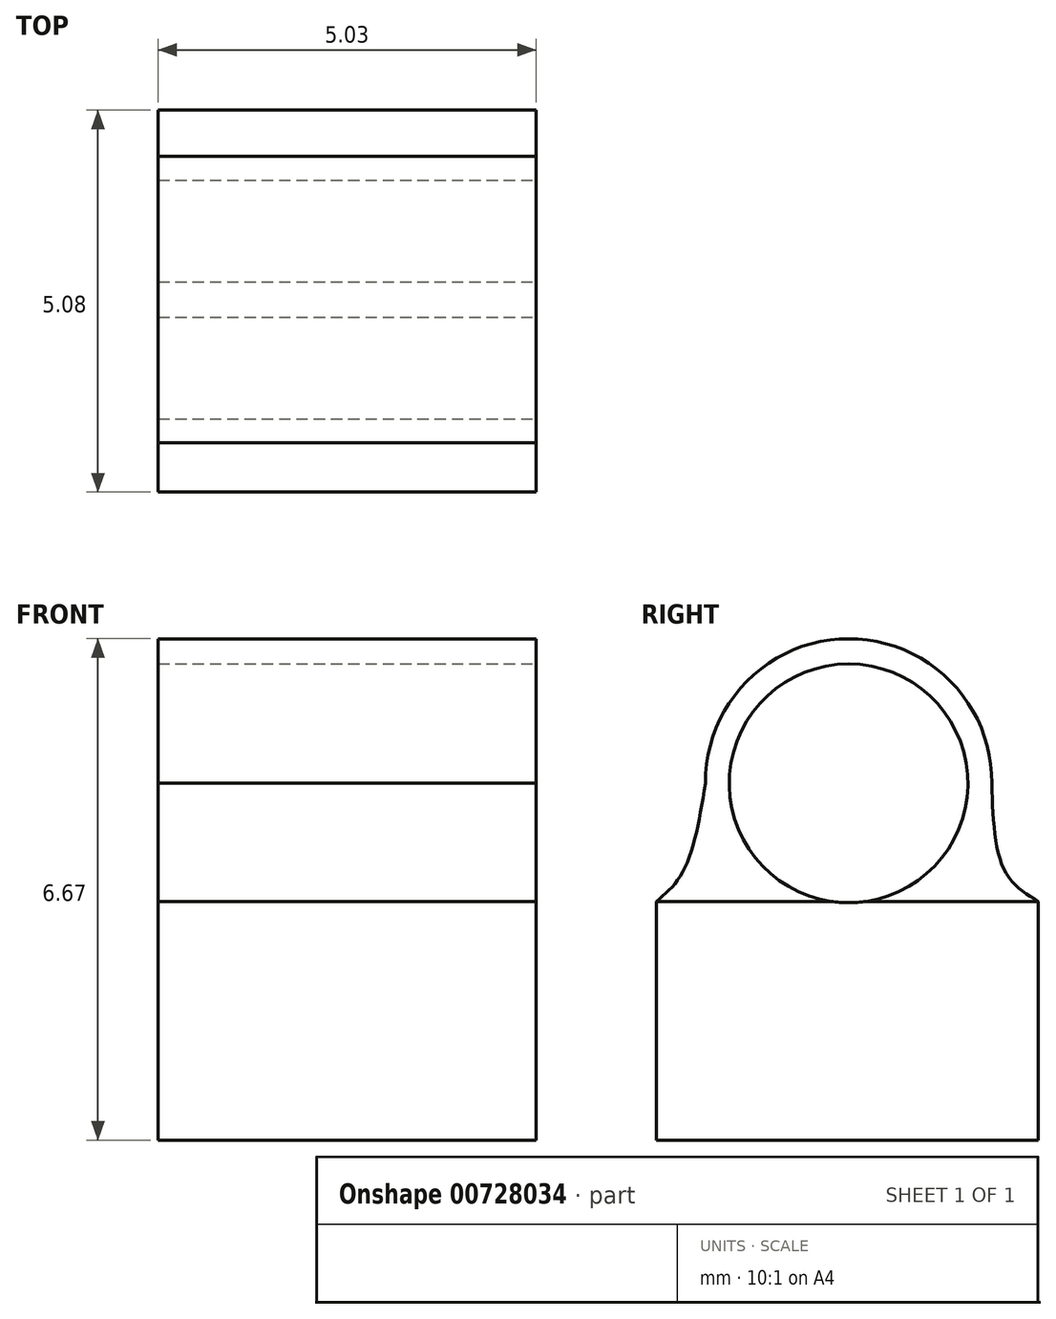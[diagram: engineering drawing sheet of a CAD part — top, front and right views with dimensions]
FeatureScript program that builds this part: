
annotation { "Feature Type Name" : "Feature", "Feature Type Description" : "" }
export const myFeature = defineFeature(function(context is Context, id is Id, definition is map)
    precondition{}
    {
        {
            var Q0;
            Q0=qCreatedBy(makeId("Top.planeOp"),FACE);
            var sketch = newSketch(context, id + "F0", { "sketchPlane" : qUnion([Q0])});
            skLineSegment(sketch, "E0.bottom", {"start": v(0, 0) * mm, "end": v(5.03, 0) * mm});
            skLineSegment(sketch, "E0.top", {"start": v(0, 5.08) * mm, "end": v(5.03, 5.08) * mm});
            skLineSegment(sketch, "E0.left", {"start": v(0, 0) * mm, "end": v(0, 5.08) * mm});
            skLineSegment(sketch, "E0.right", {"start": v(5.03, 0) * mm, "end": v(5.03, 5.08) * mm});
            skSolve(sketch);
        }
        {
            var Q0;
            Q0 = qSketchRegion(id + "F0", true);
            extrude(context, id + "F1", {"entities" : qUnion([Q0]), "depth" : 3.17 * mm, "offsetDistance" : 25.4 * mm});
        }
        {
            var Q0;
            Q0=makeQuery(id+"F1.opExtrude","SWEPT_FACE",FACE,{"disambiguationData":[OSD([sQuery(id+"F0.wireOp",EDGE,"E0.right")])]});
            var sketch = newSketch(context, id + "F2", { "sketchPlane" : qUnion([Q0])});
            skPoint(sketch, "E1.first.point", {"position": v(2.54, 3.18) * mm});
            skPoint(sketch, "E1.second.point", {"position": v(2.54, 6.35) * mm});
            skPoint(sketch, "E1.second.point.positionSnap0", {"position": v(2.54, 3.18) * mm});
            skPoint(sketch, "E1.third.point", {"position": v(0.97, 4.75) * mm});
            skArc(sketch, "E2", {"start": v(4.46, 4.75) * mm, "mid": v(2.56, 6.67) * mm, "end": v(0.65, 4.75) * mm});
            skFitSpline(sketch, "E3", {"points": [v(0, 3.18) * mm, v(0.36, 3.58) * mm, v(0.65, 4.75) * mm], "startDerivative": vector(0.97, 0.82) * mm, "endDerivative": vector(0.37, 2.22) * mm});
            skFitSpline(sketch, "E4", {"points": [v(5.08, 3.18) * mm, v(4.63, 3.58) * mm, v(4.46, 4.75) * mm], "startDerivative": vector(-1.23, 0.76) * mm, "endDerivative": vector(-0.07, 2.3) * mm});
            skSolve(sketch);
        }
        {
            var Q0;
            Q0 = qSketchRegion(id + "F2", true);
            var Q1;
            Q1=makeQuery(id+"F2.imprint","IMPRINT",FACE,{"disambiguationData":[TD([[makeQuery(id+"F2.imprint","IMPRINT",EDGE,{"derivedFrom":sQuery(id+"F2.wireOp",EDGE,"E2")}),1.0]])]});
            extrude(context, id + "F3", {"entities" : qUnion([Q0, Q1]), "oppositeDirection" : true, "depth" : 5.03 * mm, "offsetDistance" : 25.4 * mm});
        }
        {
            var Q0;
            Q0=makeQuery(id+"F3.opExtrude","CAP_FACE",FACE,{"disambiguationData":[OSD([sQuery(id+"F0.wireOp",EDGE,"E0.right"),sQuery(id+"F2.wireOp",EDGE,"E2"),sQuery(id+"F2.wireOp",EDGE,"E3"),sQuery(id+"F2.wireOp",EDGE,"E4")])],"isStart":true});
            var sketch = newSketch(context, id + "F4", { "sketchPlane" : qUnion([Q0])});
            skLineSegment(sketch, "E5", {"start": v(2.56, 6.67) * mm, "end": v(2.56, 3.18) * mm});
            skLineSegment(sketch, "E6", {"start": v(0.65, 4.75) * mm, "end": v(4.46, 4.75) * mm});
            skCircle(sketch, "E7", {"center": v(2.56, 4.75) * mm, "radius": 1.59 * mm});
            skSolve(sketch);
        }
        {
            var Q0;
            Q0 = qSketchRegion(id + "F4", true);
            extrude(context, id + "F5", {"entities" : qUnion([Q0]), "operationType" : NewBodyOperationType.REMOVE, "oppositeDirection" : true, "depth" : 5.03 * mm, "offsetDistance" : 25.4 * mm});
        }
    });
